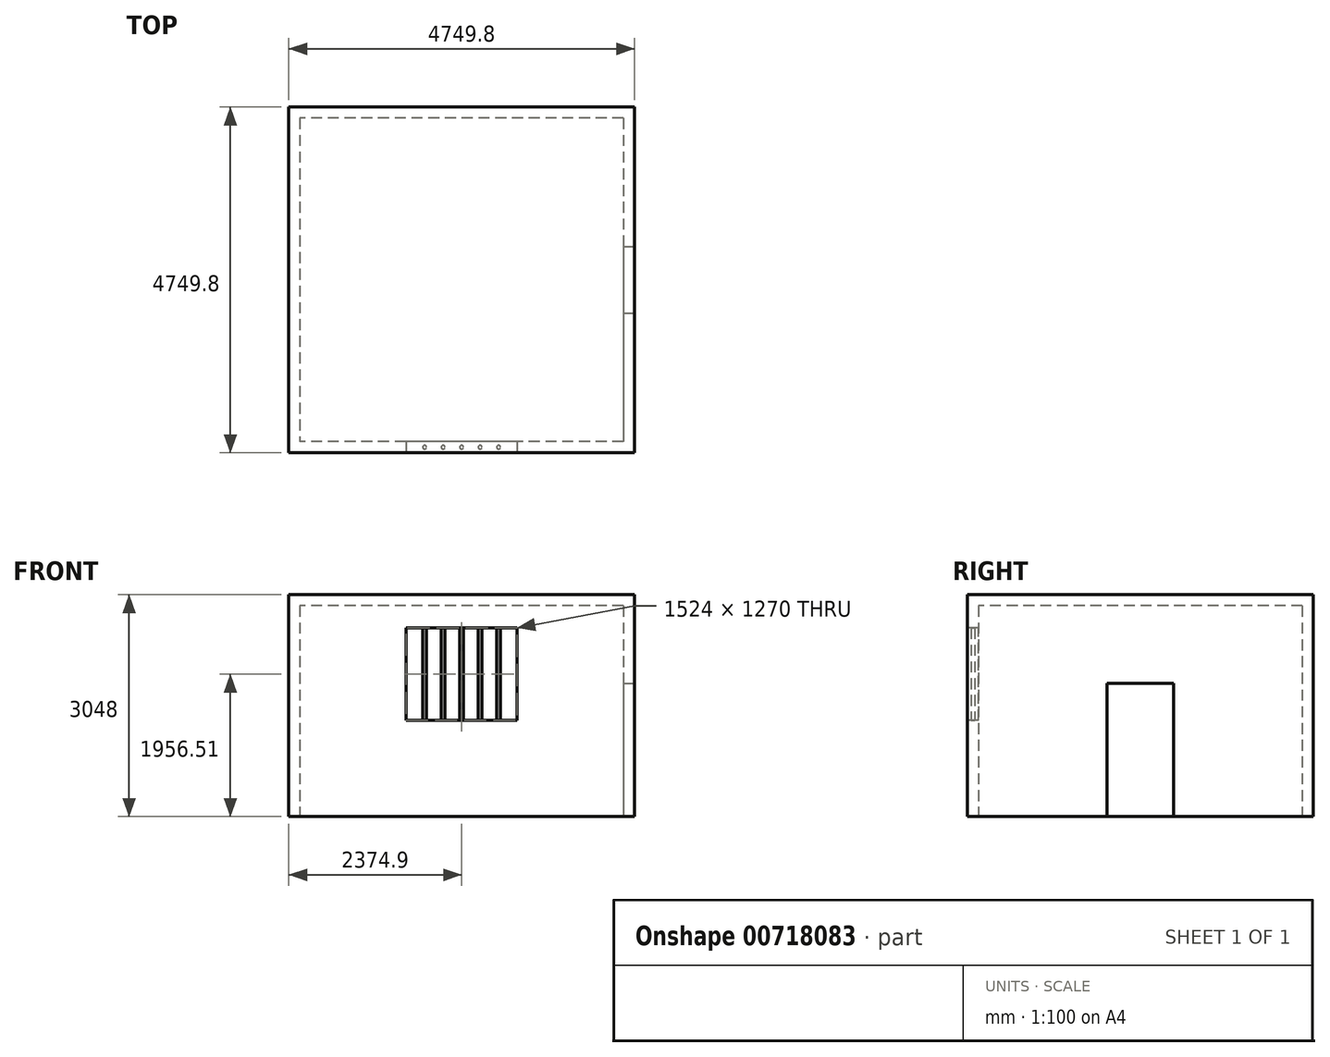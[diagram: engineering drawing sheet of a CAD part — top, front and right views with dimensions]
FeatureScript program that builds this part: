
annotation { "Feature Type Name" : "Feature", "Feature Type Description" : "" }
export const myFeature = defineFeature(function(context is Context, id is Id, definition is map)
    precondition{}
    {
        {
            var Q0;
            Q0=qCreatedBy(makeId("Top.planeOp"),FACE);
            var sketch = newSketch(context, id + "F0", { "sketchPlane" : qUnion([Q0])});
            skLineSegment(sketch, "E0.bottom", {"start": v(2374.9, -2374.9) * mm, "end": v(-2374.9, -2374.9) * mm});
            skLineSegment(sketch, "E0.top", {"start": v(2374.9, 2374.9) * mm, "end": v(-2374.9, 2374.9) * mm});
            skLineSegment(sketch, "E0.left", {"start": v(2374.9, -2374.9) * mm, "end": v(2374.9, 2374.9) * mm});
            skLineSegment(sketch, "E0.right", {"start": v(-2374.9, -2374.9) * mm, "end": v(-2374.9, 2374.9) * mm});
            skPoint(sketch, "E0.middle", {"position": v(0, 0) * mm});
            skSolve(sketch);
        }
        {
            var Q0;
            Q0=qSketchRegion(id+"F0",true);
            extrude(context, id + "F1", {"entities" : qUnion([Q0]), "depth" : 3048 * mm, "offsetDistance" : 25.4 * mm});
        }
        {
            var Q0;
            Q0=makeQuery(id+"F1.opExtrude","SWEPT_FACE",FACE,{"disambiguationData":[OSD([sQuery(id+"F0.wireOp",EDGE,"E0.bottom")])]});
            var sketch = newSketch(context, id + "F2", { "sketchPlane" : qUnion([Q0])});
            skLineSegment(sketch, "E1.bottom", {"start": v(762, 1321.51) * mm, "end": v(-762, 1321.51) * mm});
            skLineSegment(sketch, "E1.top", {"start": v(762, 2591.51) * mm, "end": v(-762, 2591.51) * mm});
            skLineSegment(sketch, "E1.left", {"start": v(762, 1321.51) * mm, "end": v(762, 2591.51) * mm});
            skLineSegment(sketch, "E1.right", {"start": v(-762, 1321.51) * mm, "end": v(-762, 2591.51) * mm});
            skPoint(sketch, "E1.middle", {"position": v(0, 1956.51) * mm});
            skSolve(sketch);
        }
        {
            var Q0;
            Q0=qSketchRegion(id+"F2",true);
            extrude(context, id + "F3", {"entities" : qUnion([Q0]), "operationType" : NewBodyOperationType.REMOVE, "oppositeDirection" : true, "depth" : 152.4 * mm, "offsetDistance" : 25.4 * mm});
        }
        {
            var Q0;
            Q0=makeQuery(id+"F1.opExtrude","CAP_FACE",FACE,{"disambiguationData":[OSD([sQuery(id+"F0.wireOp",EDGE,"E0.bottom"),sQuery(id+"F0.wireOp",EDGE,"E0.top"),sQuery(id+"F0.wireOp",EDGE,"E0.left"),sQuery(id+"F0.wireOp",EDGE,"E0.right")])],"isStart":true});
            var sketch = newSketch(context, id + "F4", { "sketchPlane" : qUnion([Q0])});
            skLineSegment(sketch, "E2.bottom", {"start": v(2222.5, -2222.5) * mm, "end": v(-2222.5, -2222.5) * mm});
            skLineSegment(sketch, "E2.top", {"start": v(2222.5, 2222.5) * mm, "end": v(-2222.5, 2222.5) * mm});
            skLineSegment(sketch, "E2.left", {"start": v(2222.5, -2222.5) * mm, "end": v(2222.5, 2222.5) * mm});
            skLineSegment(sketch, "E2.right", {"start": v(-2222.5, -2222.5) * mm, "end": v(-2222.5, 2222.5) * mm});
            skPoint(sketch, "E2.middle", {"position": v(0, 0) * mm});
            skSolve(sketch);
        }
        {
            var Q0;
            Q0=qSketchRegion(id+"F4",true);
            extrude(context, id + "F5", {"entities" : qUnion([Q0]), "operationType" : NewBodyOperationType.REMOVE, "oppositeDirection" : true, "depth" : 2895.6 * mm, "offsetDistance" : 25.4 * mm});
        }
        {
            var Q0;
            Q0=makeQuery(id+"F3.boolean.opBoolean","COPY",FACE,{"derivedFrom":makeQuery(id+"F3.opExtrude","SWEPT_FACE",FACE,{"disambiguationData":[OSD([sQuery(id+"F2.wireOp",EDGE,"E1.bottom")])]})});
            var sketch = newSketch(context, id + "F6", { "sketchPlane" : qUnion([Q0])});
            skCircle(sketch, "E3", {"center": v(-508, -2298.7) * mm, "radius": 25.4 * mm});
            skPoint(sketch, "E3.centerSnap0", {"position": v(-762, -2298.7) * mm});
            skCircle(sketch, "E4", {"center": v(0, -2298.7) * mm, "radius": 25.4 * mm});
            skCircle(sketch, "E5", {"center": v(508, -2298.7) * mm, "radius": 25.4 * mm});
            skCircle(sketch, "E6", {"center": v(-254, -2298.7) * mm, "radius": 25.4 * mm});
            skCircle(sketch, "E7", {"center": v(254, -2298.7) * mm, "radius": 25.4 * mm});
            skSolve(sketch);
        }
        {
            var Q0;
            Q0=qSketchRegion(id+"F6",true);
            extrude(context, id + "F7", {"entities" : qUnion([Q0]), "operationType" : NewBodyOperationType.ADD, "depth" : 1270 * mm, "offsetDistance" : 25.4 * mm});
        }
        {
            var Q0;
            Q0=makeQuery(id+"F1.opExtrude","SWEPT_FACE",FACE,{"disambiguationData":[OSD([sQuery(id+"F0.wireOp",EDGE,"E0.left")])]});
            var sketch = newSketch(context, id + "F8", { "sketchPlane" : qUnion([Q0])});
            skLineSegment(sketch, "E8.bottom", {"start": v(457.2, 1828.8) * mm, "end": v(-457.2, 1828.8) * mm});
            skLineSegment(sketch, "E8.top", {"start": v(457.2, -1828.8) * mm, "end": v(-457.2, -1828.8) * mm});
            skLineSegment(sketch, "E8.left", {"start": v(457.2, 1828.8) * mm, "end": v(457.2, -1828.8) * mm});
            skLineSegment(sketch, "E8.right", {"start": v(-457.2, 1828.8) * mm, "end": v(-457.2, -1828.8) * mm});
            skPoint(sketch, "E8.middle", {"position": v(0, 0) * mm});
            skSolve(sketch);
        }
        {
            var Q0;
            Q0=qSketchRegion(id+"F8",true);
            extrude(context, id + "F9", {"entities" : qUnion([Q0]), "operationType" : NewBodyOperationType.REMOVE, "oppositeDirection" : true, "depth" : 152.4 * mm, "offsetDistance" : 25.4 * mm});
        }
    });
